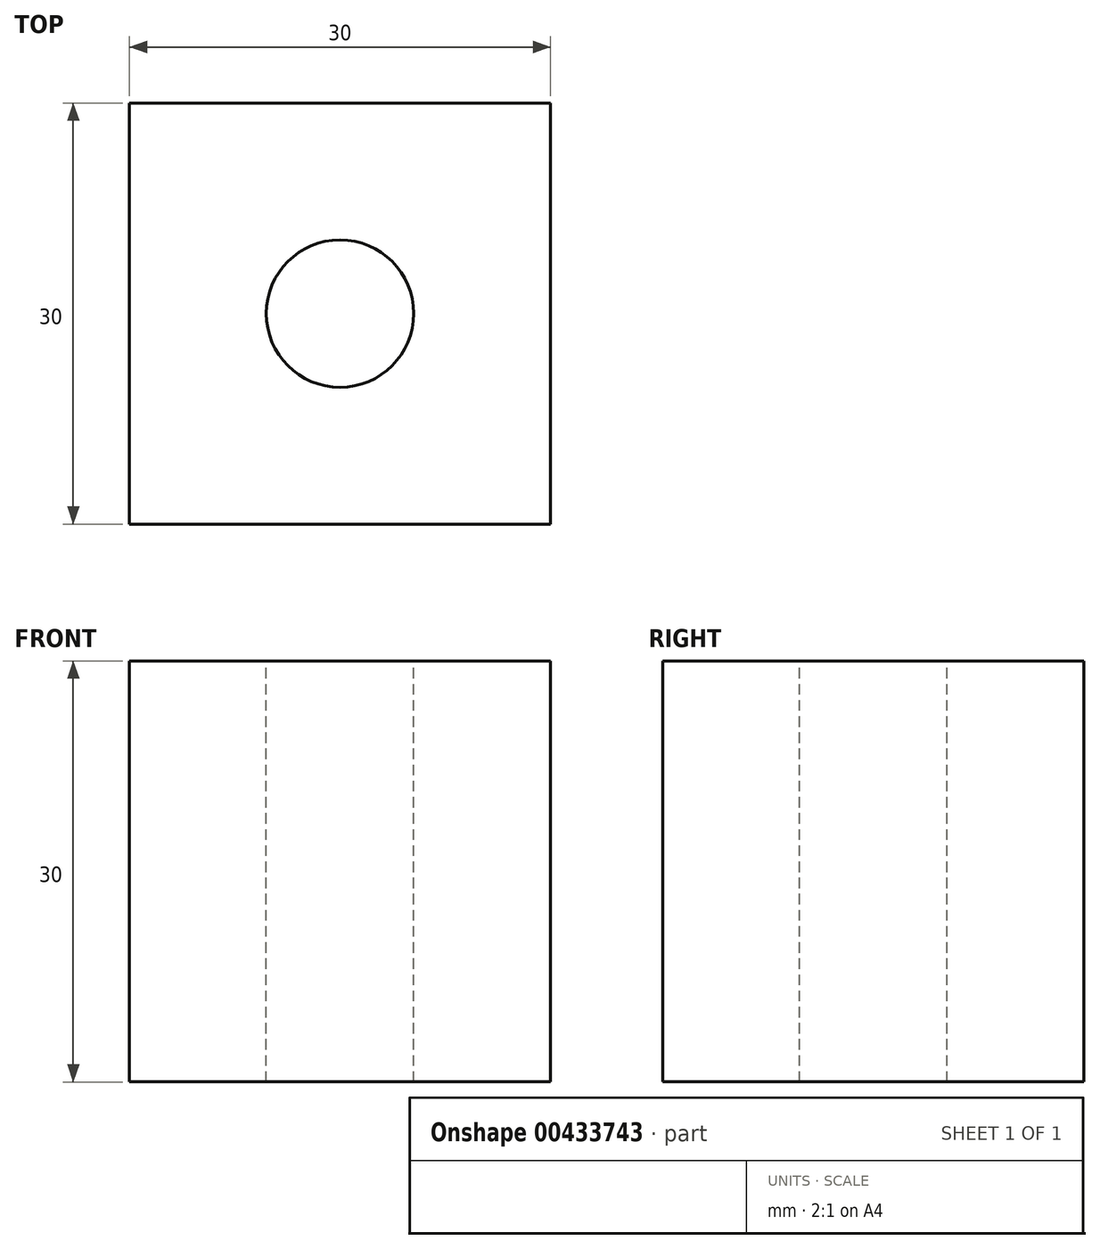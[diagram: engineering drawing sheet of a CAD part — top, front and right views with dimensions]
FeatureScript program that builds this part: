
annotation { "Feature Type Name" : "Feature", "Feature Type Description" : "" }
export const myFeature = defineFeature(function(context is Context, id is Id, definition is map)
    precondition{}
    {
        {
            var Q0;
            Q0=qCreatedBy(makeId("Front.planeOp"),FACE);
            var sketch = newSketch(context, id + "F0", { "sketchPlane" : qUnion([Q0])});
            skLineSegment(sketch, "E0.bottom", {"start": v(-30, 36.18) * mm, "end": v(0, 36.18) * mm});
            skLineSegment(sketch, "E0.top", {"start": v(-30, 6.18) * mm, "end": v(0, 6.18) * mm});
            skLineSegment(sketch, "E0.left", {"start": v(-30, 36.18) * mm, "end": v(-30, 6.18) * mm});
            skLineSegment(sketch, "E0.right", {"start": v(0, 36.18) * mm, "end": v(0, 6.18) * mm});
            skSolve(sketch);
        }
        {
            var Q0;
            Q0 = qSketchRegion(id + "F0", true);
            extrude(context, id + "F1", {"entities" : qUnion([Q0]), "depth" : 30 * mm, "offsetDistance" : 25 * mm});
        }
        {
            var Q0;
            Q0=makeQuery(id+"F1.opExtrude","SWEPT_FACE",FACE,{"disambiguationData":[OSD([sQuery(id+"F0.wireOp",EDGE,"E0.bottom")])]});
            var sketch = newSketch(context, id + "F2", { "sketchPlane" : qUnion([Q0])});
            skCircle(sketch, "E1", {"center": v(-15, -15) * mm, "radius": 5.5 * mm});
            skSolve(sketch);
        }
        {
            var Q0;
            Q0=sQuery(id+"F2.wireOp",VERTEX,"E1.center");
            var Q1;
            Q1=makeQuery(id+"F1.opExtrude","SWEPT_BODY",BODY,{"disambiguationData":[OSD([sQuery(id+"F0.wireOp",EDGE,"E0.bottom"),sQuery(id+"F0.wireOp",EDGE,"E0.top"),sQuery(id+"F0.wireOp",EDGE,"E0.left"),sQuery(id+"F0.wireOp",EDGE,"E0.right")])]});
            hole(context, id + "F3", {"style" : HoleStyle.SIMPLE, "endStyle" : HoleEndStyle.THROUGH, "holeDiameter" : 10.5 * mm, "majorDiameter" : 5 * mm, "isTappedThrough" : true, "tappedDepth" : 12 * mm, "tapClearance" : 3, "locations" : qUnion([Q0]), "scope" : qUnion([Q1])});
        }
    });
